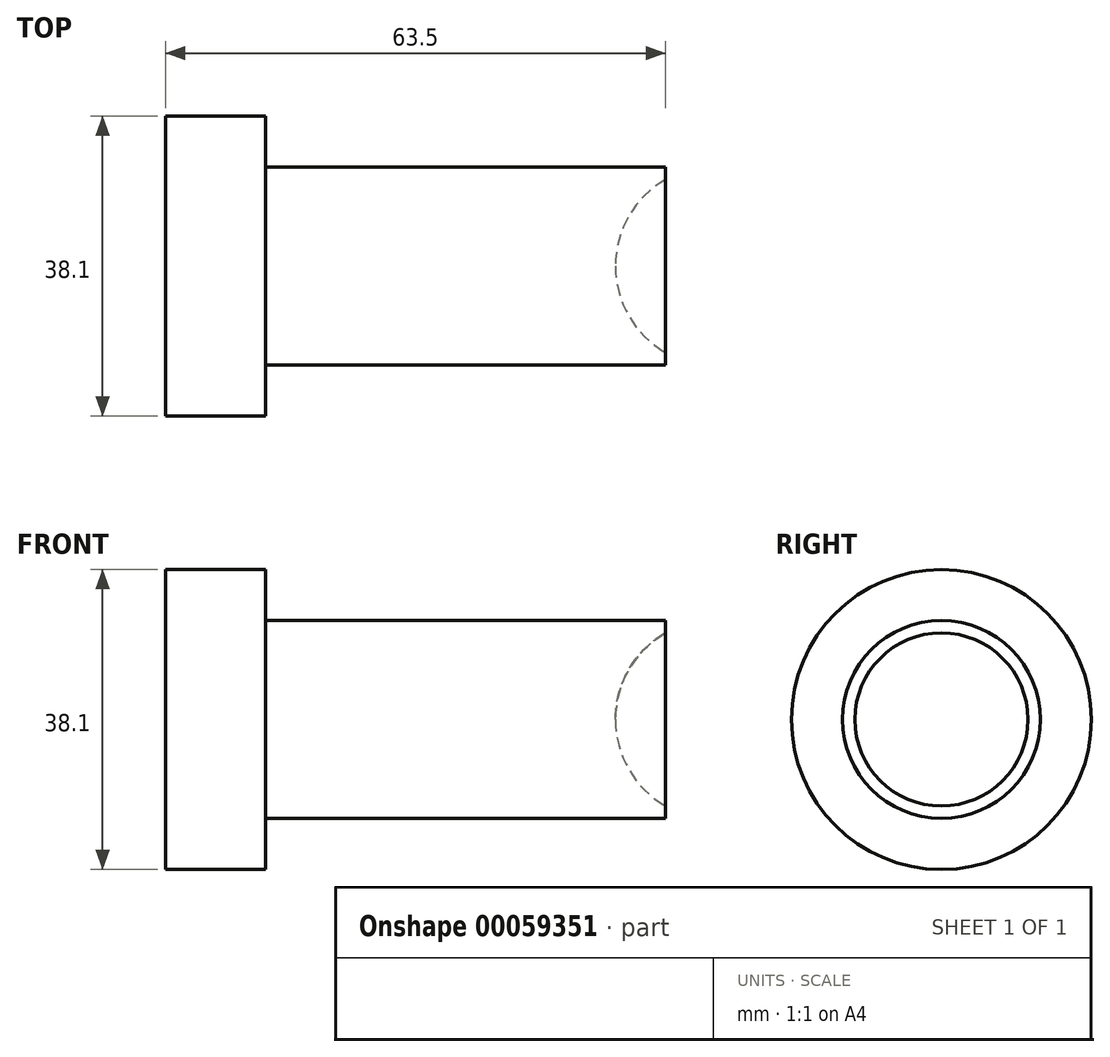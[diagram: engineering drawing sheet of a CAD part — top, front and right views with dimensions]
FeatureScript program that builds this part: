
annotation { "Feature Type Name" : "Feature", "Feature Type Description" : "" }
export const myFeature = defineFeature(function(context is Context, id is Id, definition is map)
    precondition{}
    {
        {
            var Q0;
            Q0=qCreatedBy(makeId("Right.planeOp"),FACE);
            var sketch = newSketch(context, id + "F0", { "sketchPlane" : qUnion([Q0])});
            skCircle(sketch, "E0", {"center": v(0, 0) * mm, "radius": 19.05 * mm});
            skSolve(sketch);
        }
        {
            var Q0;
            Q0=makeQuery(id+"F0.imprint","IMPRINT",FACE,{"disambiguationData":[TD([[makeQuery(id+"F0.imprint","IMPRINT",EDGE,{"derivedFrom":sQuery(id+"F0.wireOp",EDGE,"E0")}),1.0]])]});
            extrude(context, id + "F1", {"entities" : qUnion([Q0]), "oppositeDirection" : true, "depth" : 12.7 * mm});
        }
        {
            var Q0;
            Q0=qCreatedBy(makeId("Right.planeOp"),FACE);
            var sketch = newSketch(context, id + "F2", { "sketchPlane" : qUnion([Q0])});
            skCircle(sketch, "E1", {"center": v(0, 0) * mm, "radius": 12.57 * mm});
            skSolve(sketch);
        }
        {
            var Q0;
            Q0=makeQuery(id+"F2.imprint","IMPRINT",FACE,{"disambiguationData":[TD([[makeQuery(id+"F2.imprint","IMPRINT",EDGE,{"derivedFrom":sQuery(id+"F2.wireOp",EDGE,"E1")}),1.0]])]});
            extrude(context, id + "F3", {"entities" : qUnion([Q0]), "operationType" : NewBodyOperationType.ADD, "depth" : 50.8 * mm});
        }
        {
            var Q0;
            Q0=qCreatedBy(makeId("Front.planeOp"),FACE);
            var sketch = newSketch(context, id + "F4", { "sketchPlane" : qUnion([Q0])});
            skLineSegment(sketch, "E2", {"start": v(38.03, 0) * mm, "end": v(93.38, 0) * mm});
            skArc(sketch, "E3", {"start": v(69.85, 0) * mm, "mid": v(57.15, 12.7) * mm, "end": v(44.45, 0) * mm});
            skSolve(sketch);
        }
        {
            var Q0;
            {var subQ0=sQuery(id+"F4.wireOp",EDGE,"E3");Q0=makeQuery(id+"F4.imprint","IMPRINT",FACE,{"disambiguationData":[TD([[makeQuery(id+"F4.imprint","IMPRINT",EDGE,{"derivedFrom":subQ0}),1.0]])]});}
            var Q1;
            Q1=sQuery(id+"F4.wireOp",EDGE,"E2");
            revolve(context, id + "F5", {"operationType" : NewBodyOperationType.REMOVE, "entities" : qUnion([Q0]), "axis" : qUnion([Q1]), "revolveType" : RevolveType.FULL, "oppositeDirection" : true});
        }
    });
